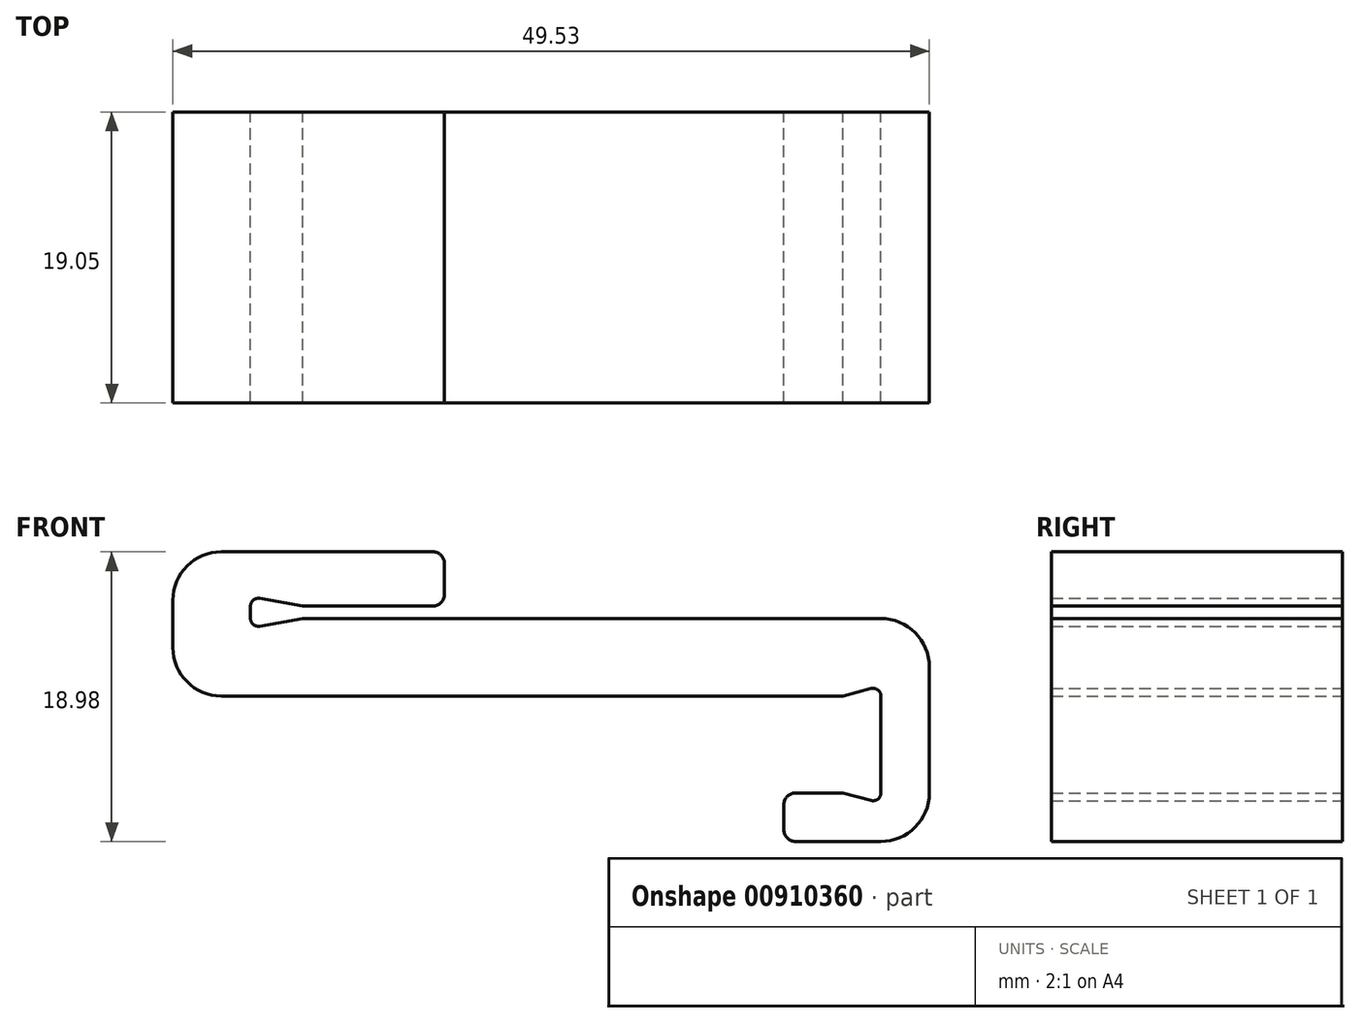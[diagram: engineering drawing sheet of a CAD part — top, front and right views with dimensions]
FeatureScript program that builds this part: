
annotation { "Feature Type Name" : "Feature", "Feature Type Description" : "" }
export const myFeature = defineFeature(function(context is Context, id is Id, definition is map)
    precondition{}
    {
        {
            var Q0;
            Q0=qCreatedBy(makeId("Front.planeOp"),FACE);
            var sketch = newSketch(context, id + "F0", { "sketchPlane" : qUnion([Q0])});
            skLineSegment(sketch, "E0", {"start": v(11.94, 0.81) * mm, "end": v(3.43, 0.81) * mm});
            skLineSegment(sketch, "E1", {"start": v(0, 0.81) * mm, "end": v(0, 0) * mm});
            skLineSegment(sketch, "E2", {"start": v(44.45, -3.17) * mm, "end": v(44.45, -11.43) * mm});
            skLineSegment(sketch, "E3", {"start": v(41.28, -14.6) * mm, "end": v(35.69, -14.6) * mm});
            skLineSegment(sketch, "E4", {"start": v(34.93, -13.84) * mm, "end": v(34.93, -12.2) * mm});
            skLineSegment(sketch, "E5", {"start": v(35.69, -11.43) * mm, "end": v(38.8, -11.43) * mm});
            skLineSegment(sketch, "E6", {"start": v(41.28, -11.43) * mm, "end": v(41.28, -5.08) * mm});
            skLineSegment(sketch, "E7", {"start": v(-5.08, -1.9) * mm, "end": v(-5.08, 1.2) * mm});
            skLineSegment(sketch, "E8", {"start": v(-1.9, 4.37) * mm, "end": v(11.94, 4.37) * mm});
            skLineSegment(sketch, "E9", {"start": v(12.7, 3.6) * mm, "end": v(12.7, 1.57) * mm});
            skArc(sketch, "E10", {"start": v(0.6, 1.31) * mm, "mid": v(0.18, 1.2) * mm, "end": v(0, 0.81) * mm});
            skArc(sketch, "E11", {"start": v(0, 0) * mm, "mid": v(0.18, -0.39) * mm, "end": v(0.6, -0.5) * mm});
            skLineSegment(sketch, "E12", {"start": v(0.6, -0.5) * mm, "end": v(3.43, 0) * mm});
            skLineSegment(sketch, "E13", {"start": v(0.6, 1.31) * mm, "end": v(3.43, 0.81) * mm});
            skLineSegment(sketch, "E14.trimOffspring", {"start": v(3.43, 0) * mm, "end": v(41.28, 0) * mm});
            skPoint(sketch, "E15.visualSharp", {"position": v(12.7, 0.81) * mm});
            skArc(sketch, "E15.filletArc", {"start": v(11.94, 0.81) * mm, "mid": v(12.48, 1.04) * mm, "end": v(12.7, 1.57) * mm});
            skPoint(sketch, "E16.visualSharp", {"position": v(12.7, 4.37) * mm});
            skArc(sketch, "E16.filletArc", {"start": v(12.7, 3.6) * mm, "mid": v(12.48, 4.15) * mm, "end": v(11.94, 4.37) * mm});
            skPoint(sketch, "E17.visualSharp", {"position": v(34.93, -11.43) * mm});
            skArc(sketch, "E17.filletArc", {"start": v(35.69, -11.43) * mm, "mid": v(35.15, -11.65) * mm, "end": v(34.93, -12.2) * mm});
            skPoint(sketch, "E18.visualSharp", {"position": v(34.93, -14.6) * mm});
            skArc(sketch, "E18.filletArc", {"start": v(34.93, -13.84) * mm, "mid": v(35.15, -14.38) * mm, "end": v(35.69, -14.6) * mm});
            skPoint(sketch, "E19.visualSharp", {"position": v(-5.08, 4.37) * mm});
            skArc(sketch, "E19.filletArc", {"start": v(-1.9, 4.37) * mm, "mid": v(-4.15, 3.44) * mm, "end": v(-5.08, 1.2) * mm});
            skPoint(sketch, "E20.visualSharp", {"position": v(-5.08, -5.08) * mm});
            skArc(sketch, "E20.filletArc", {"start": v(-5.08, -1.9) * mm, "mid": v(-4.15, -4.15) * mm, "end": v(-1.9, -5.08) * mm});
            skPoint(sketch, "E21.visualSharp", {"position": v(44.45, 0) * mm});
            skArc(sketch, "E21.filletArc", {"start": v(44.45, -3.17) * mm, "mid": v(43.52, -0.93) * mm, "end": v(41.28, 0) * mm});
            skPoint(sketch, "E22.visualSharp", {"position": v(44.45, -14.6) * mm});
            skArc(sketch, "E22.filletArc", {"start": v(41.28, -14.6) * mm, "mid": v(43.52, -13.68) * mm, "end": v(44.45, -11.43) * mm});
            skArc(sketch, "E23", {"start": v(41.28, -5.08) * mm, "mid": v(41.08, -4.68) * mm, "end": v(40.64, -4.59) * mm});
            skLineSegment(sketch, "E24", {"start": v(40.64, -4.59) * mm, "end": v(38.8, -5.08) * mm});
            skArc(sketch, "E25", {"start": v(40.64, -11.92) * mm, "mid": v(41.08, -11.83) * mm, "end": v(41.28, -11.43) * mm});
            skLineSegment(sketch, "E26", {"start": v(40.64, -11.92) * mm, "end": v(38.8, -11.43) * mm});
            skLineSegment(sketch, "E27.trimOffspring", {"start": v(38.8, -5.08) * mm, "end": v(-1.9, -5.08) * mm});
            skSolve(sketch);
        }
        {
            var Q0;
            Q0 = qSketchRegion(id + "F0", true);
            extrude(context, id + "F1", {"entities" : qUnion([Q0]), "depth" : 19.05 * mm, "offsetDistance" : 25.4 * mm});
        }
    });
